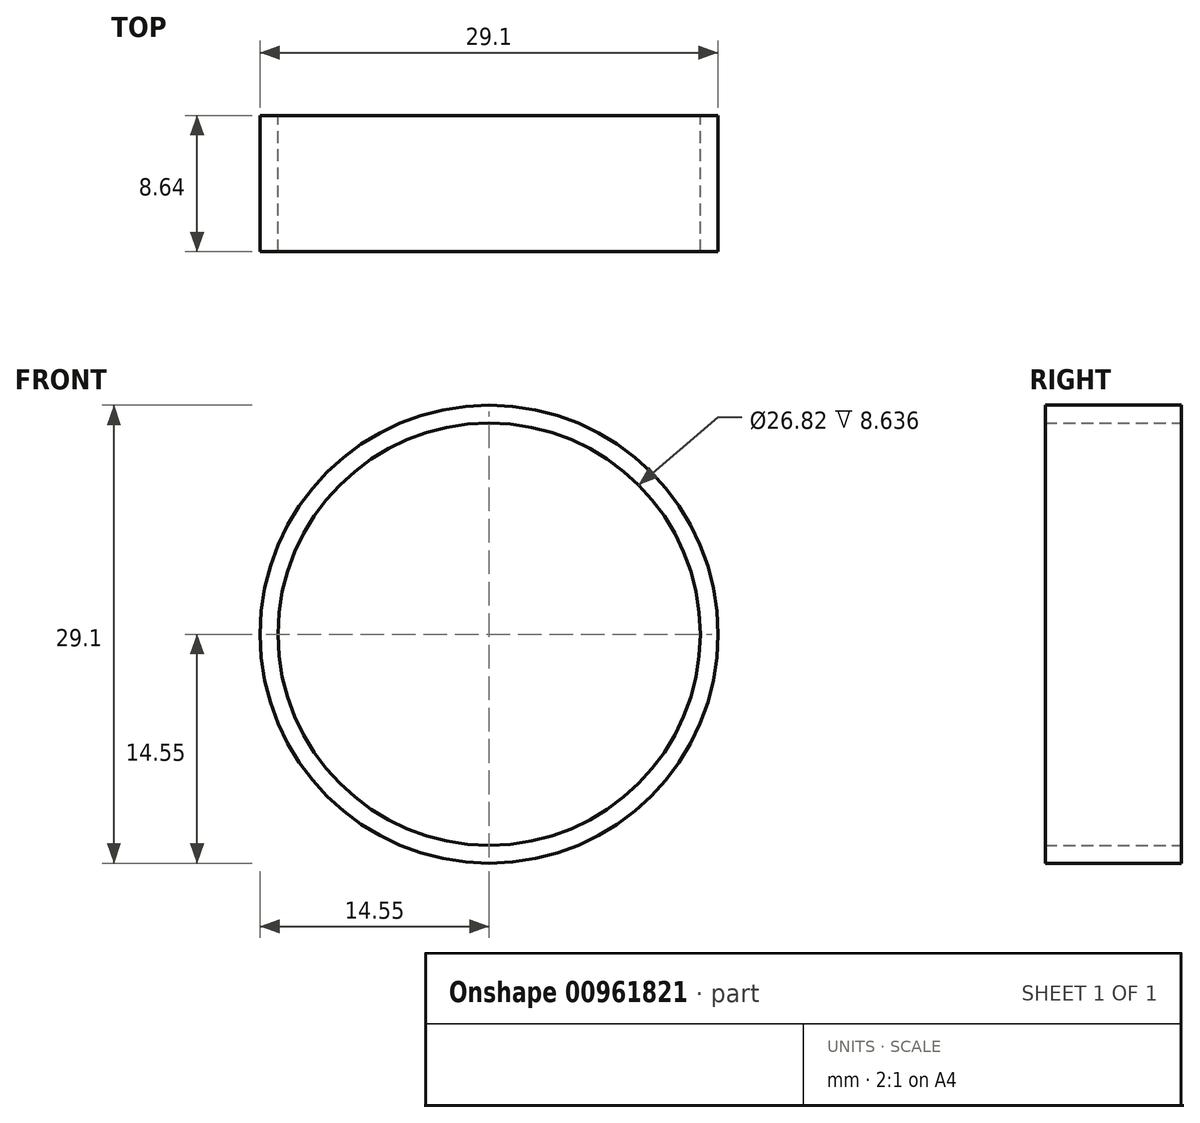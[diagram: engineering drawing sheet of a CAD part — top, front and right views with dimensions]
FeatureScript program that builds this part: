
annotation { "Feature Type Name" : "Feature", "Feature Type Description" : "" }
export const myFeature = defineFeature(function(context is Context, id is Id, definition is map)
    precondition{}
    {
        {
            var Q0;
            Q0=qCreatedBy(makeId("Front.planeOp"),FACE);
            var sketch = newSketch(context, id + "F0", { "sketchPlane" : qUnion([Q0])});
            skCircle(sketch, "E0", {"center": v(0, 0) * mm, "radius": 14.55 * mm});
            skCircle(sketch, "E1", {"center": v(0, 0) * mm, "radius": 13.41 * mm});
            skSolve(sketch);
        }
        {
            var Q0;
            Q0=makeQuery(id+"F0.imprint","IMPRINT",FACE,{"disambiguationData":[TD([[makeQuery(id+"F0.imprint","IMPRINT",EDGE,{"derivedFrom":sQuery(id+"F0.wireOp",EDGE,"E0")}),1.0]])]});
            extrude(context, id + "F1", {"entities" : qUnion([Q0]), "depth" : 8.64 * mm, "offsetDistance" : 25.4 * mm});
        }
    });
